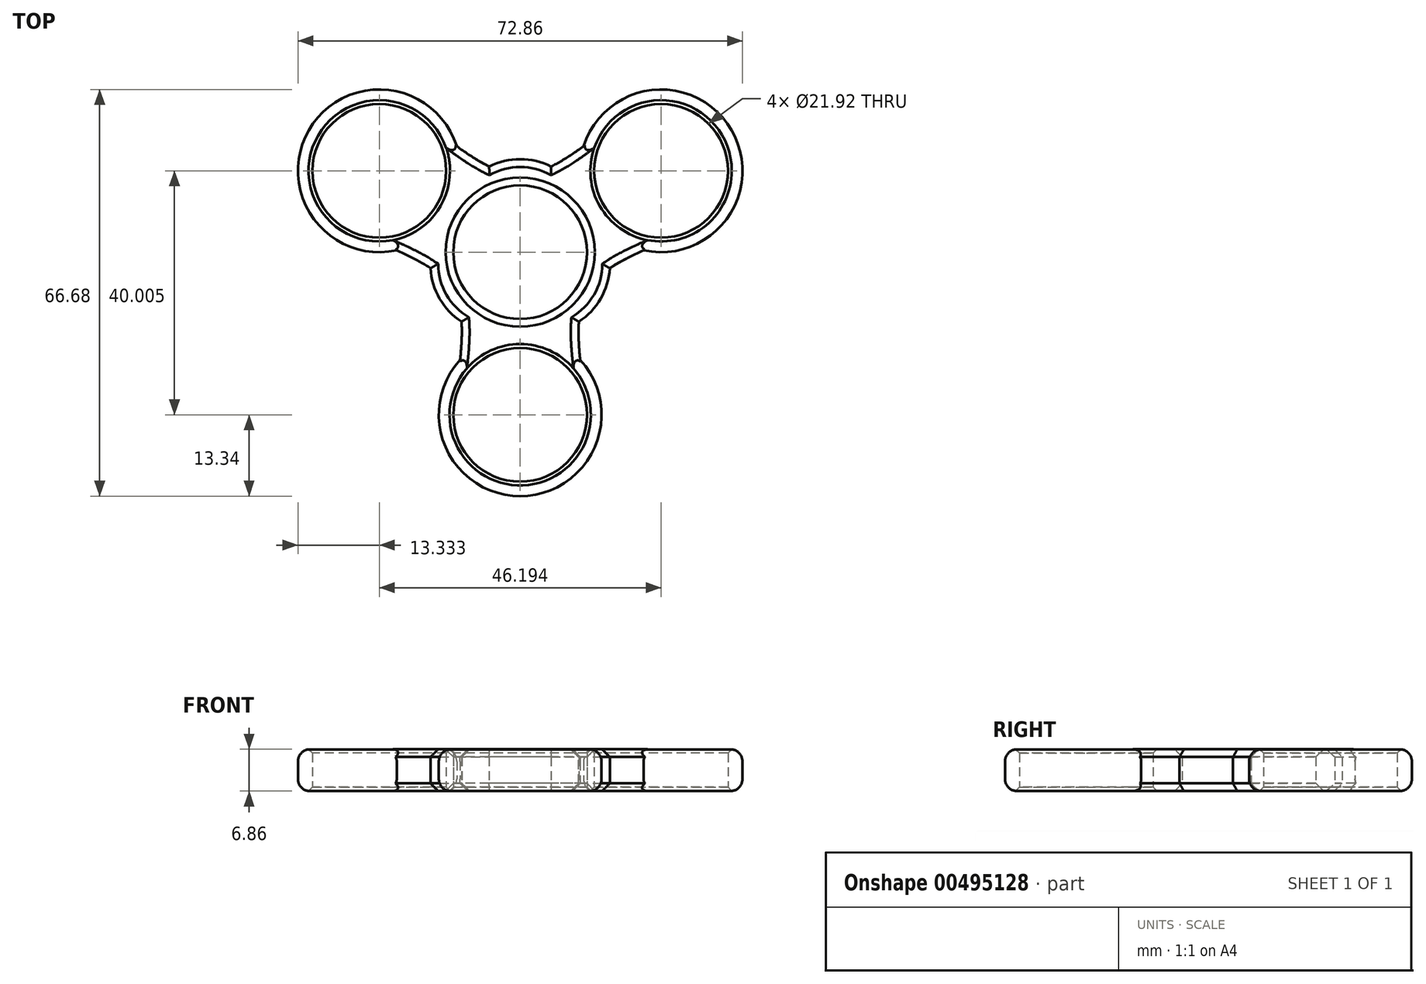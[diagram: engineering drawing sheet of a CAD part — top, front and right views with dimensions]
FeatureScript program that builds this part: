
annotation { "Feature Type Name" : "Feature", "Feature Type Description" : "" }
export const myFeature = defineFeature(function(context is Context, id is Id, definition is map)
    precondition{}
    {
        {
            var Q0;
            Q0=qCreatedBy(makeId("Top.planeOp"),FACE);
            var sketch = newSketch(context, id + "F0", { "sketchPlane" : qUnion([Q0])});
            skCircle(sketch, "E0", {"center": v(0, 0) * mm, "radius": 10.96 * mm});
            skCircle(sketch, "E1", {"center": v(0, 0) * mm, "radius": 12.7 * mm});
            skLineSegment(sketch, "E2", {"start": v(0, 0) * mm, "end": v(0, -12.7) * mm});
            skCircle(sketch, "E3.cCircle", {"center": v(0, 0) * mm, "radius": 12.7 * mm, "construction": true});
            skLineSegment(sketch, "E3.0", {"start": v(0, -12.7) * mm, "end": v(-11, 6.35) * mm});
            skLineSegment(sketch, "E3.1", {"start": v(-11, 6.35) * mm, "end": v(11, 6.35) * mm});
            skLineSegment(sketch, "E3.2", {"start": v(11, 6.35) * mm, "end": v(0, -12.7) * mm});
            skLineSegment(sketch, "E4", {"start": v(-11, 6.35) * mm, "end": v(0, 0) * mm});
            skLineSegment(sketch, "E5", {"start": v(0, 0) * mm, "end": v(11, 6.35) * mm});
            skLineSegment(sketch, "E6", {"start": v(-11, 6.35) * mm, "end": v(-23.1, 13.34) * mm});
            skLineSegment(sketch, "E7", {"start": v(11, 6.35) * mm, "end": v(23.1, 13.34) * mm});
            skLineSegment(sketch, "E8", {"start": v(0, -12.7) * mm, "end": v(0, -26.67) * mm});
            skCircle(sketch, "E9", {"center": v(-23.1, 13.33) * mm, "radius": 10.96 * mm});
            skCircle(sketch, "E10", {"center": v(23.1, 13.34) * mm, "radius": 10.96 * mm});
            skCircle(sketch, "E11", {"center": v(0, -26.67) * mm, "radius": 10.96 * mm});
            skLineSegment(sketch, "E12", {"start": v(-23.1, 13.33) * mm, "end": v(-28.58, 3.84) * mm});
            skLineSegment(sketch, "E13", {"start": v(-23.1, 13.33) * mm, "end": v(-17.62, 22.83) * mm});
            skLineSegment(sketch, "E14", {"start": v(23.1, 13.34) * mm, "end": v(17.62, 22.83) * mm});
            skLineSegment(sketch, "E15", {"start": v(23.1, 13.34) * mm, "end": v(28.58, 3.84) * mm});
            skLineSegment(sketch, "E16", {"start": v(0, -26.67) * mm, "end": v(-10.96, -26.67) * mm});
            skLineSegment(sketch, "E17", {"start": v(0, -26.67) * mm, "end": v(10.96, -26.67) * mm});
            skCircle(sketch, "E18", {"center": v(-23.1, 13.33) * mm, "radius": 13.34 * mm});
            skCircle(sketch, "E19", {"center": v(23.1, 13.34) * mm, "radius": 13.34 * mm});
            skCircle(sketch, "E20", {"center": v(0, -26.67) * mm, "radius": 13.34 * mm});
            skPoint(sketch, "E21", {"position": v(-5.5, -3.17) * mm});
            skPoint(sketch, "E22", {"position": v(0, 6.35) * mm});
            skPoint(sketch, "E23", {"position": v(5.5, -3.18) * mm});
            skLineSegment(sketch, "E24", {"start": v(-11, -6.35) * mm, "end": v(-13.18, -7.64) * mm});
            skLineSegment(sketch, "E25", {"start": v(11, -6.35) * mm, "end": v(13.2, -7.62) * mm});
            skArc(sketch, "E26", {"start": v(-11, 6.35) * mm, "mid": v(-13.2, -7.62) * mm, "end": v(0, -12.7) * mm});
            skArc(sketch, "E27", {"start": v(0, -12.7) * mm, "mid": v(13.2, -7.62) * mm, "end": v(11, 6.35) * mm});
            skLineSegment(sketch, "E28", {"start": v(0, 12.7) * mm, "end": v(0, 15.24) * mm});
            skArc(sketch, "E29", {"start": v(11, 6.35) * mm, "mid": v(0, 15.24) * mm, "end": v(-11, 6.35) * mm});
            skFitSpline(sketch, "E30", {"points": [v(-28.58, 3.84) * mm, v(-11, -6.35) * mm, v(-10.96, -26.67) * mm], "startDerivative": vector(52.41, -22.24) * mm, "endDerivative": vector(-6.95, -56.51) * mm});
            skFitSpline(sketch, "E31", {"points": [v(10.96, -26.67) * mm, v(11, -6.35) * mm, v(28.58, 3.84) * mm], "startDerivative": vector(-6.95, 56.51) * mm, "endDerivative": vector(52.41, 22.24) * mm});
            skFitSpline(sketch, "E32", {"points": [v(17.62, 22.83) * mm, v(0, 12.7) * mm, v(-17.62, 22.83) * mm], "startDerivative": vector(-45.47, -34.27) * mm, "endDerivative": vector(-45.47, 34.27) * mm});
            skSolve(sketch);
        }
        {
            var Q0;
            Q0=qSketchRegion(id+"F0",true);
            var Q1;
            {var subQ1=sQuery(id+"F0.wireOp",EDGE,"E3.0");var subQ4=sQuery(id+"F0.wireOp",EDGE,"E0");var subQ8=makeQuery(id+"F0.imprint","INTERSECT",VERTEX,{"disambiguationData":[OD(0.0)],"derivedFrom":[subQ4,subQ1]});Q1=makeQuery(id+"F0.imprint","IMPRINT",FACE,{"disambiguationData":[TD([[makeQuery(id+"F0.imprint","IMPRINT",EDGE,{"disambiguationData":[TD([[subQ8,-1.0]])],"derivedFrom":subQ4}),-1.0]])]});}
            var Q2;
            {var subQ1=sQuery(id+"F0.wireOp",EDGE,"E3.1");var subQ4=sQuery(id+"F0.wireOp",EDGE,"E0");var subQ8=makeQuery(id+"F0.imprint","INTERSECT",VERTEX,{"disambiguationData":[OD(0.0)],"derivedFrom":[subQ4,subQ1]});Q2=makeQuery(id+"F0.imprint","IMPRINT",FACE,{"disambiguationData":[TD([[makeQuery(id+"F0.imprint","IMPRINT",EDGE,{"disambiguationData":[TD([[subQ8,-1.0]])],"derivedFrom":subQ4}),-1.0]])]});}
            var Q3;
            {var subQ1=sQuery(id+"F0.wireOp",EDGE,"E3.2");var subQ6=sQuery(id+"F0.wireOp",EDGE,"E0");var subQ8=makeQuery(id+"F0.imprint","INTERSECT",VERTEX,{"disambiguationData":[OD(0.0)],"derivedFrom":[subQ6,subQ1]});Q3=makeQuery(id+"F0.imprint","IMPRINT",FACE,{"disambiguationData":[TD([[makeQuery(id+"F0.imprint","IMPRINT",EDGE,{"disambiguationData":[TD([[subQ8,1.0]])],"derivedFrom":subQ6}),-1.0]])]});}
            var Q4;
            {var subQ0=sQuery(id+"F0.wireOp",EDGE,"E2");var subQ1=sQuery(id+"F0.wireOp",EDGE,"E0");var subQ2=makeQuery(id+"F0.imprint","INTERSECT",VERTEX,{"derivedFrom":[subQ1,subQ0]});Q4=makeQuery(id+"F0.imprint","IMPRINT",FACE,{"disambiguationData":[TD([[makeQuery(id+"F0.imprint","IMPRINT",EDGE,{"disambiguationData":[TD([[subQ2,-1.0]])],"derivedFrom":subQ1}),-1.0]])]});}
            var Q5;
            {var subQ0=sQuery(id+"F0.wireOp",EDGE,"E3.0");var subQ1=sQuery(id+"F0.wireOp",EDGE,"E0");var subQ2=makeQuery(id+"F0.imprint","INTERSECT",VERTEX,{"disambiguationData":[OD(1.0)],"derivedFrom":[subQ1,subQ0]});Q5=makeQuery(id+"F0.imprint","IMPRINT",FACE,{"disambiguationData":[TD([[makeQuery(id+"F0.imprint","IMPRINT",EDGE,{"disambiguationData":[TD([[subQ2,-1.0]])],"derivedFrom":subQ1}),-1.0]])]});}
            var Q6;
            {var subQ0=sQuery(id+"F0.wireOp",EDGE,"E5");var subQ1=sQuery(id+"F0.wireOp",EDGE,"E0");var subQ2=makeQuery(id+"F0.imprint","INTERSECT",VERTEX,{"derivedFrom":[subQ1,subQ0]});Q6=makeQuery(id+"F0.imprint","IMPRINT",FACE,{"disambiguationData":[TD([[makeQuery(id+"F0.imprint","IMPRINT",EDGE,{"disambiguationData":[TD([[subQ2,1.0]])],"derivedFrom":subQ1}),-1.0]])]});}
            var Q7;
            {var subQ0=sQuery(id+"F0.wireOp",EDGE,"E5");var subQ1=sQuery(id+"F0.wireOp",EDGE,"E0");var subQ2=makeQuery(id+"F0.imprint","INTERSECT",VERTEX,{"derivedFrom":[subQ1,subQ0]});Q7=makeQuery(id+"F0.imprint","IMPRINT",FACE,{"disambiguationData":[TD([[makeQuery(id+"F0.imprint","IMPRINT",EDGE,{"disambiguationData":[TD([[subQ2,-1.0]])],"derivedFrom":subQ1}),-1.0]])]});}
            var Q8;
            {var subQ0=sQuery(id+"F0.wireOp",EDGE,"E4");var subQ1=sQuery(id+"F0.wireOp",EDGE,"E0");var subQ2=makeQuery(id+"F0.imprint","INTERSECT",VERTEX,{"derivedFrom":[subQ1,subQ0]});Q8=makeQuery(id+"F0.imprint","IMPRINT",FACE,{"disambiguationData":[TD([[makeQuery(id+"F0.imprint","IMPRINT",EDGE,{"disambiguationData":[TD([[subQ2,-1.0]])],"derivedFrom":subQ1}),-1.0]])]});}
            var Q9;
            {var subQ0=sQuery(id+"F0.wireOp",EDGE,"E3.1");var subQ1=sQuery(id+"F0.wireOp",EDGE,"E0");var subQ2=makeQuery(id+"F0.imprint","INTERSECT",VERTEX,{"disambiguationData":[OD(1.0)],"derivedFrom":[subQ1,subQ0]});Q9=makeQuery(id+"F0.imprint","IMPRINT",FACE,{"disambiguationData":[TD([[makeQuery(id+"F0.imprint","IMPRINT",EDGE,{"disambiguationData":[TD([[subQ2,-1.0]])],"derivedFrom":subQ1}),-1.0]])]});}
            extrude(context, id + "F1", {"entities" : qUnion([Q0, Q1, Q2, Q3, Q4, Q5, Q6, Q7, Q8, Q9]), "depth" : 6.86 * mm, "offsetDistance" : 25.4 * mm});
        }
        {
            var Q0;
            Q0=makeQuery(id+"F1.opExtrude","CAP_EDGE",EDGE,{"disambiguationData":[OSD([sQuery(id+"F0.wireOp",EDGE,"E0")])],"isStart":true});
            var Q1;
            Q1=makeQuery(id+"F1.opExtrude","CAP_EDGE",EDGE,{"disambiguationData":[OSD([sQuery(id+"F0.wireOp",EDGE,"E0")])],"isStart":false});
            chamfer(context, id + "F2", {"entities" : qUnion([Q0, Q1]), "width" : 1.27 * mm, "tangentPropagation" : true});
        }
        {
            var Q0;
            {var subQ0=sQuery(id+"F0.wireOp",EDGE,"E31");Q0=makeQuery(id+"F1.opExtrude","CAP_EDGE",EDGE,{"disambiguationData":[OSD([subQ0]),TDD([makeQuery(id+"F0.imprint","IMPRINT",EDGE,{"disambiguationData":[TD([[makeQuery(id+"F0.imprint","INTERSECT",VERTEX,{"derivedFrom":[sQuery(id+"F0.wireOp",EDGE,"E20"),subQ0]}),-1.0]])],"derivedFrom":subQ0})])],"isStart":false});}
            var Q1;
            Q1=makeQuery(id+"F1.opExtrude","CAP_EDGE",EDGE,{"disambiguationData":[OSD([sQuery(id+"F0.wireOp",EDGE,"E27")])],"isStart":false});
            var Q2;
            {var subQ0=sQuery(id+"F0.wireOp",EDGE,"E31");Q2=makeQuery(id+"F1.opExtrude","CAP_EDGE",EDGE,{"disambiguationData":[OSD([subQ0]),TDD([makeQuery(id+"F0.imprint","IMPRINT",EDGE,{"disambiguationData":[TD([[makeQuery(id+"F0.imprint","INTERSECT",VERTEX,{"derivedFrom":[sQuery(id+"F0.wireOp",EDGE,"E19"),subQ0]}),1.0]])],"derivedFrom":subQ0})])],"isStart":false});}
            var Q3;
            {var subQ0=sQuery(id+"F0.wireOp",EDGE,"E32");Q3=makeQuery(id+"F1.opExtrude","CAP_EDGE",EDGE,{"disambiguationData":[OSD([subQ0]),TDD([makeQuery(id+"F0.imprint","IMPRINT",EDGE,{"disambiguationData":[TD([[makeQuery(id+"F0.imprint","INTERSECT",VERTEX,{"derivedFrom":[sQuery(id+"F0.wireOp",EDGE,"E19"),subQ0]}),-1.0]])],"derivedFrom":subQ0})])],"isStart":false});}
            var Q4;
            Q4=makeQuery(id+"F1.opExtrude","CAP_EDGE",EDGE,{"disambiguationData":[OSD([sQuery(id+"F0.wireOp",EDGE,"E29")])],"isStart":false});
            var Q5;
            {var subQ0=sQuery(id+"F0.wireOp",EDGE,"E32");Q5=makeQuery(id+"F1.opExtrude","CAP_EDGE",EDGE,{"disambiguationData":[OSD([subQ0]),TDD([makeQuery(id+"F0.imprint","IMPRINT",EDGE,{"disambiguationData":[TD([[makeQuery(id+"F0.imprint","INTERSECT",VERTEX,{"derivedFrom":[sQuery(id+"F0.wireOp",EDGE,"E18"),subQ0]}),1.0]])],"derivedFrom":subQ0})])],"isStart":false});}
            var Q6;
            {var subQ0=sQuery(id+"F0.wireOp",EDGE,"E30");Q6=makeQuery(id+"F1.opExtrude","CAP_EDGE",EDGE,{"disambiguationData":[OSD([subQ0]),TDD([makeQuery(id+"F0.imprint","IMPRINT",EDGE,{"disambiguationData":[TD([[makeQuery(id+"F0.imprint","INTERSECT",VERTEX,{"derivedFrom":[sQuery(id+"F0.wireOp",EDGE,"E18"),subQ0]}),-1.0]])],"derivedFrom":subQ0})])],"isStart":false});}
            var Q7;
            {var subQ0=sQuery(id+"F0.wireOp",EDGE,"E30");Q7=makeQuery(id+"F1.opExtrude","CAP_EDGE",EDGE,{"disambiguationData":[OSD([subQ0]),TDD([makeQuery(id+"F0.imprint","IMPRINT",EDGE,{"disambiguationData":[TD([[makeQuery(id+"F0.imprint","INTERSECT",VERTEX,{"derivedFrom":[sQuery(id+"F0.wireOp",EDGE,"E18"),subQ0]}),-1.0]])],"derivedFrom":subQ0})])],"isStart":true});}
            var Q8;
            Q8=makeQuery(id+"F1.opExtrude","CAP_EDGE",EDGE,{"disambiguationData":[OSD([sQuery(id+"F0.wireOp",EDGE,"E26")])],"isStart":true});
            var Q9;
            Q9=makeQuery(id+"F1.opExtrude","CAP_EDGE",EDGE,{"disambiguationData":[OSD([sQuery(id+"F0.wireOp",EDGE,"E26")])],"isStart":false});
            var Q10;
            {var subQ0=sQuery(id+"F0.wireOp",EDGE,"E30");Q10=makeQuery(id+"F1.opExtrude","CAP_EDGE",EDGE,{"disambiguationData":[OSD([subQ0]),TDD([makeQuery(id+"F0.imprint","IMPRINT",EDGE,{"disambiguationData":[TD([[makeQuery(id+"F0.imprint","INTERSECT",VERTEX,{"derivedFrom":[sQuery(id+"F0.wireOp",EDGE,"E20"),subQ0]}),1.0]])],"derivedFrom":subQ0})])],"isStart":true});}
            var Q11;
            {var subQ0=sQuery(id+"F0.wireOp",EDGE,"E30");Q11=makeQuery(id+"F1.opExtrude","CAP_EDGE",EDGE,{"disambiguationData":[OSD([subQ0]),TDD([makeQuery(id+"F0.imprint","IMPRINT",EDGE,{"disambiguationData":[TD([[makeQuery(id+"F0.imprint","INTERSECT",VERTEX,{"derivedFrom":[sQuery(id+"F0.wireOp",EDGE,"E20"),subQ0]}),1.0]])],"derivedFrom":subQ0})])],"isStart":false});}
            var Q12;
            {var subQ0=sQuery(id+"F0.wireOp",EDGE,"E31");Q12=makeQuery(id+"F1.opExtrude","CAP_EDGE",EDGE,{"disambiguationData":[OSD([subQ0]),TDD([makeQuery(id+"F0.imprint","IMPRINT",EDGE,{"disambiguationData":[TD([[makeQuery(id+"F0.imprint","INTERSECT",VERTEX,{"derivedFrom":[sQuery(id+"F0.wireOp",EDGE,"E20"),subQ0]}),-1.0]])],"derivedFrom":subQ0})])],"isStart":true});}
            var Q13;
            Q13=makeQuery(id+"F1.opExtrude","CAP_EDGE",EDGE,{"disambiguationData":[OSD([sQuery(id+"F0.wireOp",EDGE,"E27")])],"isStart":true});
            var Q14;
            {var subQ0=sQuery(id+"F0.wireOp",EDGE,"E31");Q14=makeQuery(id+"F1.opExtrude","CAP_EDGE",EDGE,{"disambiguationData":[OSD([subQ0]),TDD([makeQuery(id+"F0.imprint","IMPRINT",EDGE,{"disambiguationData":[TD([[makeQuery(id+"F0.imprint","INTERSECT",VERTEX,{"derivedFrom":[sQuery(id+"F0.wireOp",EDGE,"E19"),subQ0]}),1.0]])],"derivedFrom":subQ0})])],"isStart":true});}
            var Q15;
            {var subQ0=sQuery(id+"F0.wireOp",EDGE,"E32");Q15=makeQuery(id+"F1.opExtrude","CAP_EDGE",EDGE,{"disambiguationData":[OSD([subQ0]),TDD([makeQuery(id+"F0.imprint","IMPRINT",EDGE,{"disambiguationData":[TD([[makeQuery(id+"F0.imprint","INTERSECT",VERTEX,{"derivedFrom":[sQuery(id+"F0.wireOp",EDGE,"E19"),subQ0]}),-1.0]])],"derivedFrom":subQ0})])],"isStart":true});}
            var Q16;
            Q16=makeQuery(id+"F1.opExtrude","CAP_EDGE",EDGE,{"disambiguationData":[OSD([sQuery(id+"F0.wireOp",EDGE,"E29")])],"isStart":true});
            var Q17;
            {var subQ0=sQuery(id+"F0.wireOp",EDGE,"E32");Q17=makeQuery(id+"F1.opExtrude","CAP_EDGE",EDGE,{"disambiguationData":[OSD([subQ0]),TDD([makeQuery(id+"F0.imprint","IMPRINT",EDGE,{"disambiguationData":[TD([[makeQuery(id+"F0.imprint","INTERSECT",VERTEX,{"derivedFrom":[sQuery(id+"F0.wireOp",EDGE,"E18"),subQ0]}),1.0]])],"derivedFrom":subQ0})])],"isStart":true});}
            chamfer(context, id + "F3", {"entities" : qUnion([Q0, Q1, Q2, Q3, Q4, Q5, Q6, Q7, Q8, Q9, Q10, Q11, Q12, Q13, Q14, Q15, Q16, Q17]), "width" : 1.27 * mm, "tangentPropagation" : true});
        }
        {
            var Q0;
            Q0=makeQuery(id+"F1.opExtrude","CAP_EDGE",EDGE,{"disambiguationData":[OSD([sQuery(id+"F0.wireOp",EDGE,"E19")])],"isStart":false});
            var Q1;
            Q1=makeQuery(id+"F1.opExtrude","CAP_EDGE",EDGE,{"disambiguationData":[OSD([sQuery(id+"F0.wireOp",EDGE,"E19")])],"isStart":true});
            var Q2;
            Q2=makeQuery(id+"F1.opExtrude","CAP_EDGE",EDGE,{"disambiguationData":[OSD([sQuery(id+"F0.wireOp",EDGE,"E18")])],"isStart":false});
            var Q3;
            Q3=makeQuery(id+"F1.opExtrude","CAP_EDGE",EDGE,{"disambiguationData":[OSD([sQuery(id+"F0.wireOp",EDGE,"E18")])],"isStart":true});
            var Q4;
            Q4=makeQuery(id+"F1.opExtrude","CAP_EDGE",EDGE,{"disambiguationData":[OSD([sQuery(id+"F0.wireOp",EDGE,"E20")])],"isStart":false});
            var Q5;
            Q5=makeQuery(id+"F1.opExtrude","CAP_EDGE",EDGE,{"disambiguationData":[OSD([sQuery(id+"F0.wireOp",EDGE,"E20")])],"isStart":true});
            fillet(context, id + "F4", {"entities" : qUnion([Q0, Q1, Q2, Q3, Q4, Q5]), "radius" : 1.98 * mm, "tangentPropagation" : true, "allowEdgeOverflow" : false});
        }
        {
            var Q0;
            Q0=makeQuery(id+"F1.opExtrude","CAP_EDGE",EDGE,{"disambiguationData":[OSD([sQuery(id+"F0.wireOp",EDGE,"E10")])],"isStart":true});
            var Q1;
            Q1=makeQuery(id+"F1.opExtrude","CAP_EDGE",EDGE,{"disambiguationData":[OSD([sQuery(id+"F0.wireOp",EDGE,"E9")])],"isStart":true});
            var Q2;
            Q2=makeQuery(id+"F1.opExtrude","CAP_EDGE",EDGE,{"disambiguationData":[OSD([sQuery(id+"F0.wireOp",EDGE,"E9")])],"isStart":false});
            var Q3;
            Q3=makeQuery(id+"F1.opExtrude","CAP_EDGE",EDGE,{"disambiguationData":[OSD([sQuery(id+"F0.wireOp",EDGE,"E10")])],"isStart":false});
            var Q4;
            Q4=makeQuery(id+"F1.opExtrude","CAP_EDGE",EDGE,{"disambiguationData":[OSD([sQuery(id+"F0.wireOp",EDGE,"E11")])],"isStart":false});
            var Q5;
            Q5=makeQuery(id+"F1.opExtrude","CAP_EDGE",EDGE,{"disambiguationData":[OSD([sQuery(id+"F0.wireOp",EDGE,"E11")])],"isStart":true});
            chamfer(context, id + "F5", {"entities" : qUnion([Q0, Q1, Q2, Q3, Q4, Q5]), "width" : 0.64 * mm, "tangentPropagation" : true});
        }
    });
